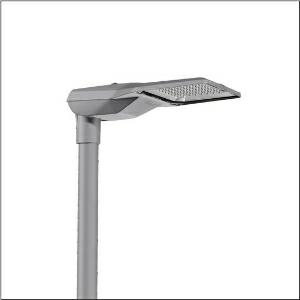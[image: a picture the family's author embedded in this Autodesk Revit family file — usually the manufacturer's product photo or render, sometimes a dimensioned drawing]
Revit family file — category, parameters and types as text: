
# Revit family: streetlight_sl_21_iq_midi___st1_0a_5xe3d31v08nb_ec4a
name_source: partatom
category: Lighting Fixtures
units: mm (PartAtom-declared; Revit-internal decimal feet)

## family parameters
Cut with Voids When Loaded = No
Host = Face
Light Source = No
Part Type = Normal
Room Calculation Point = No
Round Connector Dimension = Use Diameter
Shared = No

## types (1)
- --- (1 x LED, 21550 lm, 136.6 W, 3000K)
    Apparent Load = 137 VA
    CIE Flux Codes = 40 73 97 100 100
    Color Rendering = 70
    Color Temperature = 3000K
    Default Elevation = 1800 mm
    Description = Streetlight SL 21 iQ midi, mast luminaire, primary light control with lens, of PMMA, primary optical cover: cover, of toughened safety glass, transparent, light distribution: ST1.0a, light emission: direct distribution, primary light characteristic: asymmetric, installation type: post-top, side-entry, LED, High Power LED, rated luminous flux: 21.550lm, luminous efficacy: 158lm/W, light colour: 730, colour temperature: 3000K, control gear: iQ-Street Remote, D4i with power reduction, control: pre-setting: logarithmic dimming characteristic, Street-Remote, Auto-Match, Temp-Guard, Lumen-Switch, Night-Set, Smart-Wire, Light-Fading, Desk-Remote (wireless, voltage-free reading and setting of iQ features in the workshop via application-optimized NFC function/RFID function), optimised constant luminous flux control (CLO 2.0), mains connection: 230..240V, AC, 50/60Hz, start of lifetime: 137W, end of service life: 144W, reduction: 61W, luminaire housing, of diecast aluminium, powder-coated, Siteco® metallic grey (DB 702S), corrosivity category C5 mid according to DIN EN ISO 12944, please order mast flange separately, inclination adjustable: 0°, 5°, 10°, 15°, sealing non-destructively replaceable, multi-level sealing system, length: 644mm, width: 335mm, height: 110mm, mast flange for spigot size: 42mm (side-entry): 5XC10008XM4, 60/48mm (side-entry/post-top): 5XC10108XM2, 76/60mm (side-entry/post-top): 5XC10108XM1, mounting height: 4..8m, Smart Interface above, protection rating (complete): IP66, insulation class (complete): insulation class II (safety insulation), certification: CE, ENEC, ENEC+, VDE, impact resistance: IK10, permissible operating ambient temperature for outdoor applications: -40..+50°C, standard-compliant lighting for roads and squares, packaging unit: 1 piece

Light Distribution: ST1.0a
    Height = 111 mm
    Lamp = 1 x LED
    Lamp Light Flux = 21550 lm
    Lamp Power = 136.6 W
    Lamp count = 1
    Length = 644 mm
    Luminous efficacy = 158 lm/W
    Manufacturer = Siteco
    ModVariant = No
    Model = 5XE3D31V08NB
    Number of Poles = 1
    OnlyDefault = Yes
    Power Factor = 1
    Product Name = Streetlight SL 21 iQ midi | ST1.0a
    Product group = mast luminaire | pylon top
    ProductGroupID = 6100
    Protection Class = Protection class II
    Protection Degree = IP 66
    RLX_Detail_Level = 1
    RLX_Emergency_Light_Flux = 0 lm
    RLX_Emergency_Type = 0
    RLX_Emergency_Type_DB = No
    RlxData = <blob elided: 90725 chars, md5=58919022>
    Socket = socket
    Standby Power = 0 W
    System Light Flux = 21550 lm
    System Power = 137 W
    Type Comments = factory setting: luminous flux: 100 % | dim-lin: 254 | 733 mA
    Type Image = l_1004302.jpg
    URL = http://relux.com
    VarID = @adj_135397
    Voltage = 0 V
    Weight = 0.00 kg
    Width = 336 mm

## geometry (parser evidence)
native form markers: Blend x4, Sweep x12
no freeform markers — native parametric forms only
